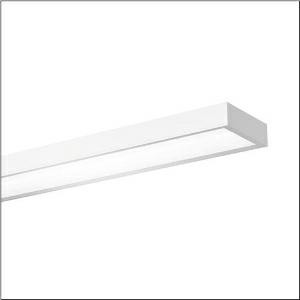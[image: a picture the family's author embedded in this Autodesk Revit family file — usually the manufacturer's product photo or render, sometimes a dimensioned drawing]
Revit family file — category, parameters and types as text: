
# Revit family: sport_31_51hs12dc4eca
name_source: partatom
category: Lighting Fixtures
units: mm (PartAtom-declared; Revit-internal decimal feet)

## family parameters
Cut with Voids When Loaded = No
Host = Face
Light Source = No
Part Type = Normal
Room Calculation Point = No
Round Connector Dimension = Use Diameter
Shared = No

## types (1)
- --- (1 x LED, 11990 lm, 89.4 W, 4000K)
    Apparent Load = 89 VA
    CIE Flux Codes = 65 89 97 100 100
    Color Rendering = 80
    Color Temperature = 4000K
    Default Elevation = 1800 mm
    Description = Sport 31, LED high bay luminaire, primary light control with reflector, of sheet steel, primary anti-glare with prismatic structure, of PC, primary optical cover: cover panel, of PC, light emission: direct distribution, primary light characteristic: symmetric, installation type: suspended mounting, recessed, surface-mounted, LED, rated luminous flux: 12.000lm, luminous efficacy: 137lm/W, light colour: 840, colour temperature: 4000K, control gear: ECG DALI, with terminal, 5-pole, max. 2.5mm², mains connection: 220..240V, AC, 50/60Hz, rated input power: 88W, housing, of sheet steel, traffic white (RAL 9016), length: 1.540mm, width: 315mm, height: 95mm, protection rating (complete): IP20, protection rating (lamp compartment, on room side): IP50, insulation class (complete): insulation class I (protective earthing), certification: CE, ENEC, UKCA, ball protection: ball impact resistant with ceiling mounting or chain suspension, impact resistance: IK08, permissible operating ambient temperature: -20..+35°C, standard: DIN 18032-3, packaging unit: 1 piece
    Height = 100 mm  [stored 0.328084 ft]
    Lamp = 1 x LED
    Lamp Light Flux = 11990 lm
    Lamp Power = 89.4 W
    Lamp count = 1
    Length = 1500 mm
    Luminous efficacy = 134 lm/W
    Manufacturer = Siteco
    ModVariant = No
    Model = 51HS12DC4ECA
    Mounting Place = Ceiling
    Mounting Type = Pendant
    Number of Poles = 1
    OnlyDefault = Yes
    Power Factor = 1
    Product Name = Sport 31
    Product group = LED high bay luminaire
    ProductGroupID = 903
    Protection Class = Protection class I
    Protection Degree = IP 20
    RLX_Detail_Level = 1
    RlxData = <blob elided: 22781 chars, md5=3eb5ee2f>
    Socket = socket
    Standby Power = 0 W
    System Light Flux = 11990 lm
    System Power = 89 W
    Type Comments = factory setting: luminous flux: 100 % | dim-lin: 254 | 380 mA
    Type Image = l_1006823.jpg
    URL = http://relux.com
    VarID = @adj_121101
    Voltage = 0 V
    Weight = 0.00 kg
    Width = 315 mm

note: [stored X ft] marks values corroborated as IEEE doubles in the binary element streams (Revit-internal decimal feet)

## geometry (parser evidence)
native form markers: Blend x4, Sweep x11
no freeform markers — native parametric forms only
